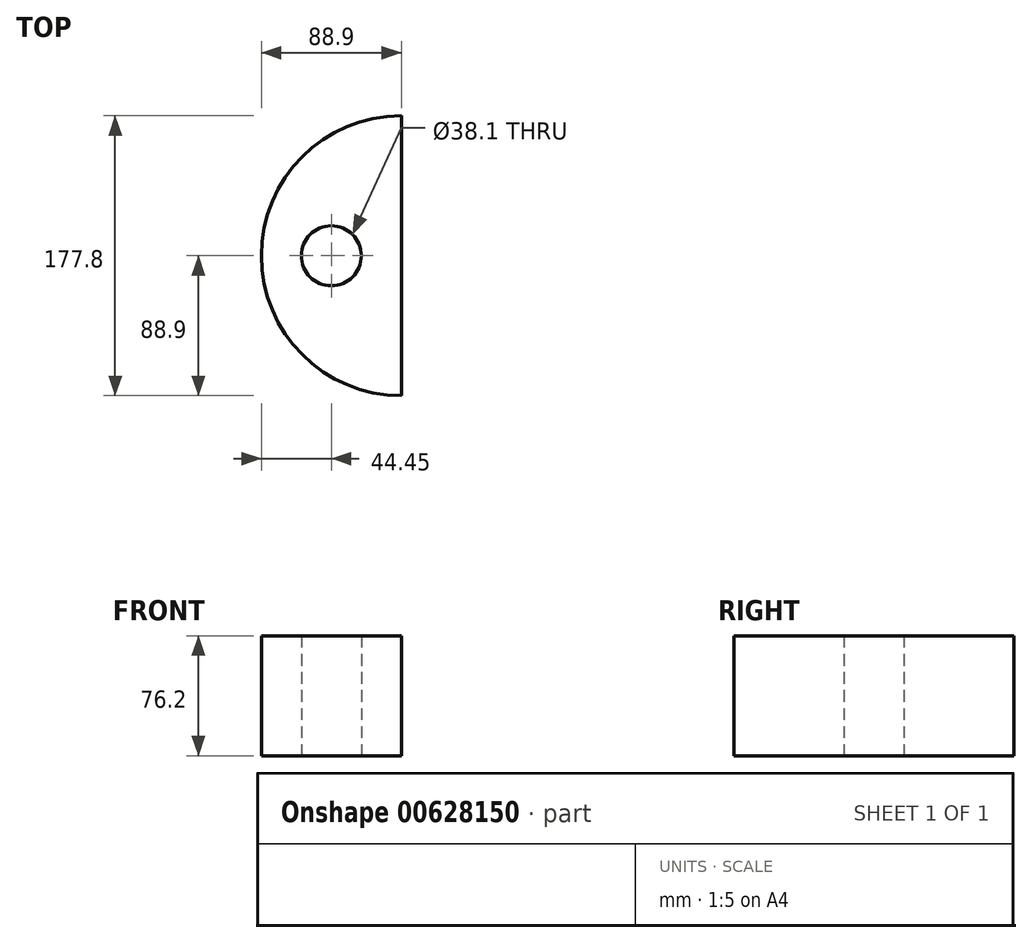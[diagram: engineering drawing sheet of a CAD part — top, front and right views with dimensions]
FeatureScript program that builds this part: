
annotation { "Feature Type Name" : "Feature", "Feature Type Description" : "" }
export const myFeature = defineFeature(function(context is Context, id is Id, definition is map)
    precondition{}
    {
        {
            var Q0;
            Q0=qCreatedBy(makeId("Top.planeOp"),FACE);
            var sketch = newSketch(context, id + "F0", { "sketchPlane" : qUnion([Q0])});
            skArc(sketch, "E0", {"start": v(0, 88.9) * mm, "mid": v(-88.9, 0) * mm, "end": v(0, -88.9) * mm});
            skLineSegment(sketch, "E1", {"start": v(0, 88.9) * mm, "end": v(0, -88.9) * mm});
            skLineSegment(sketch, "E2", {"start": v(0, 0) * mm, "end": v(-88.9, 0) * mm});
            skCircle(sketch, "E3", {"center": v(-44.45, 0) * mm, "radius": 19.05 * mm});
            skSolve(sketch);
        }
        {
            var Q0;
            {var subQ1=sQuery(id+"F0.wireOp",EDGE,"E1");var subQ5=sQuery(id+"F0.wireOp",EDGE,"E0");var subQ6=makeQuery(id+"F0.imprint","INTERSECT",VERTEX,{"disambiguationData":[OD(1.0)],"derivedFrom":[subQ5,subQ1]});Q0=makeQuery(id+"F0.imprint","IMPRINT",FACE,{"disambiguationData":[TD([[makeQuery(id+"F0.imprint","IMPRINT",EDGE,{"disambiguationData":[TD([[subQ6,1.0]])],"derivedFrom":subQ5}),1.0]])]});}
            var Q1;
            {var subQ1=sQuery(id+"F0.wireOp",EDGE,"E0");var subQ5=sQuery(id+"F0.wireOp",EDGE,"E1");var subQ8=makeQuery(id+"F0.imprint","INTERSECT",VERTEX,{"disambiguationData":[OD(0.0)],"derivedFrom":[subQ1,subQ5]});Q1=makeQuery(id+"F0.imprint","IMPRINT",FACE,{"disambiguationData":[TD([[makeQuery(id+"F0.imprint","IMPRINT",EDGE,{"disambiguationData":[TD([[subQ8,-1.0]])],"derivedFrom":subQ1}),1.0]])]});}
            extrude(context, id + "F1", {"entities" : qUnion([Q0, Q1]), "depth" : 76.2 * mm, "offsetDistance" : 25.4 * mm});
        }
    });
